FCSTD DOCUMENT  (FreeCAD 1.0R39109 (Git))
Label: TriggerPlateAssembly
License: All rights reserved
LicenseURL: http://en.wikipedia.org/wiki/All_rights_reserved
objects: App::Link×11, App::Part×1
EXTERNAL_REF file=../../ReferenceParts/KW-12.FCStd obj=Part
EXTERNAL_REF file=../../ReferenceParts/M3.FCStd obj=Part
EXTERNAL_REF file=../../ReferenceParts/M2.FCStd obj=Part
EXTERNAL_REF file=TriggerPlate.stl.FCStd obj=Part001
EXTERNAL_REF file=TriggerAssembly.FCStd obj=Assembly
EXTERNAL_REF file=LoadingLeverAssembly.FCStd obj=Part

FEATURE [App::Link] Link008  label="KW-12-25mm - Loading"
  LinkPlacement = pos=(48,-22,0) rot=(0,0,1;0.349066rad)
  LinkedObject = -> <external ../../ReferenceParts/KW-12.FCStd>#Part
  Placement = pos=(48,-22,0) rot=(0,0,1;0.349066rad)
FEATURE [App::Link] Link009  label="KW-12-25mm - Trigger"
  LinkPlacement = pos=(14,-11,2e-16) rot=(0,0,1;2.87979rad)
  LinkedObject = -> <external ../../ReferenceParts/KW-12.FCStd>#Part
  Placement = pos=(14,-11,2e-16) rot=(0,0,1;2.87979rad)
FEATURE [App::Link] Link  label="M3x10"
  LinkPlacement = pos=(30,-36,3.2) rot=(0,0,1;3.14159rad)
  LinkedObject = -> <external ../../ReferenceParts/M3.FCStd>#Part
  Placement = pos=(30,-36,3.2) rot=(0,0,1;3.14159rad)
FEATURE [App::Link] Link010  label="M3x011"
  LinkPlacement = pos=(35,-6,3.2) rot=(0,0,1;3.14177rad)
  LinkedObject = -> <external ../../ReferenceParts/M3.FCStd>#Part
  Placement = pos=(35,-6,3.2) rot=(0,0,1;3.14177rad)
FEATURE [App::Link] Link016  label="M2x10"
  LinkPlacement = pos=(8.66128,-12.5718,3.25) rot=(0,0,-1;0.261799rad)
  LinkedObject = -> <external ../../ReferenceParts/M2.FCStd>#Part
  Placement = pos=(8.66128,-12.5718,3.25) rot=(0,0,-1;0.261799rad)
FEATURE [App::Link] TriggerPlate_stl  label="TriggerPlate.stl001"
  LinkedObject = -> <external TriggerPlate.stl.FCStd>#Part001
FEATURE [App::Link] Link017  label="TriggerAssembly"
  LinkPlacement = pos=(30,-36,0.2) rot=(0,0,1;0rad)
  LinkedObject = -> <external TriggerAssembly.FCStd>#Assembly
  Placement = pos=(30,-36,0.2) rot=(0,0,1;0rad)
FEATURE [App::Link] M2x10  label="M2x011"
  LinkPlacement = pos=(17.8376,-15.0306,3.25) rot=(0,0,1;2.87979rad)
  LinkedObject = -> <external ../../ReferenceParts/M2.FCStd>#Part
  Placement = pos=(17.8376,-15.0306,3.25) rot=(0,0,1;2.87979rad)
FEATURE [App::Link] M2x011  label="M2x012"
  LinkPlacement = pos=(42.5446,-20.8995,3.25) rot=(0,0,1;0.349066rad)
  LinkedObject = -> <external ../../ReferenceParts/M2.FCStd>#Part
  Placement = pos=(42.5446,-20.8995,3.25) rot=(0,0,1;0.349066rad)
FEATURE [App::Link] M2x012  label="M2x013"
  LinkPlacement = pos=(51.4717,-17.6503,3.25) rot=(0,0,1;3.49066rad)
  LinkedObject = -> <external ../../ReferenceParts/M2.FCStd>#Part
  Placement = pos=(51.4717,-17.6503,3.25) rot=(0,0,1;3.49066rad)
FEATURE [App::Link] Link018  label="LoadingLeverAssembly"
  LinkPlacement = pos=(35,-6,0) rot=(0,0,1;0rad)
  LinkedObject = -> <external LoadingLeverAssembly.FCStd>#Part
  Placement = pos=(35,-6,0) rot=(0,0,1;0rad)
FEATURE [App::Part] Part  label="TriggerPlateAssembly"
  Group = -> [Link,Link009,Link016,Link010,Link008,TriggerPlate_stl,Link017,M2x10,M2x011,M2x012,Link018]
  Origin = -> Origin

RESOLVED EXTERNAL PARTS (link-assembly join: the EXTERNAL_REF files above that resolve inside this repo's crawl, each included once):
---- part ../../ReferenceParts/KW-12.FCStd = doc fcstd_e4d357ee2f76 ----
FCSTD DOCUMENT  (FreeCAD 1.0R39109 (Git))
Label: KW-12
License: All rights reserved
LicenseURL: http://en.wikipedia.org/wiki/All_rights_reserved
objects: Sketcher::SketchObject×6, PartDesign::Body×6, PartDesign::Pad×5, PartDesign::Mirrored×2, PartDesign::FeatureBase×2, PartDesign::Pocket×1, App::Part×1
note: 44 computed .brp shape members not serialized (recipe doc carries the construction recipe); baked Part::Feature solids carry a one-line shape summary decoded from their .brp

FEATURE [Sketcher::SketchObject] Sketch
  ArcFitTolerance = 1e-06
  AttachmentSupport = -> [XY_Plane]
  FullyConstrained = true
  MakeInternals = false
  MapMode = 5
  sketch-geometry (16):
    g0: LineSegment StartX=10 StartY=0.4 StartZ=0 EndX=10 EndY=10.4 EndZ=0
    g1: LineSegment StartX=-10 StartY=10 StartZ=0 EndX=-10 EndY=0.4 EndZ=0
    g2: LineSegment StartX=10 StartY=10.4 StartZ=0 EndX=-1.2008e-12 EndY=10.4 EndZ=0
    g3: LineSegment StartX=-1.2011e-12 StartY=10.4 StartZ=0 EndX=-1.2011e-12 EndY=10 EndZ=0
    g4: LineSegment StartX=-1.2011e-12 StartY=10 StartZ=0 EndX=-10 EndY=10 EndZ=0
    g5: LineSegment StartX=-10 StartY=0.4 StartZ=0 EndX=-6.75 EndY=0.4 EndZ=0
    g6: LineSegment StartX=-6.75 StartY=0.4 StartZ=0 EndX=-6.75 EndY=1.2024e-12 EndZ=0
    g7: LineSegment StartX=-6.75 StartY=1.2024e-12 StartZ=0 EndX=-2.75 EndY=1.2024e-12 EndZ=0
    g8: LineSegment StartX=-2.75 StartY=1.2024e-12 StartZ=0 EndX=-2.75 EndY=0.4 EndZ=0
    g9: LineSegment StartX=-2.75 StartY=0.4 StartZ=0 EndX=2.75 EndY=0.4 EndZ=0
    g10: LineSegment StartX=2.75 StartY=0.4 StartZ=0 EndX=2.75 EndY=-1.2024e-12 EndZ=0
    g11: LineSegment StartX=2.75 StartY=-1.2024e-12 StartZ=0 EndX=6.75 EndY=-1.2024e-12 EndZ=0
    g12: LineSegment StartX=6.75 StartY=-1.2024e-12 StartZ=0 EndX=6.75 EndY=0.4 EndZ=0
    g13: LineSegment StartX=6.75 StartY=0.4 StartZ=0 EndX=10 EndY=0.4 EndZ=0
    g14: GeomPoint X=-4.75 Y=1.2024e-12 Z=0
    g15: GeomPoint X=-4.75 Y=2.9 Z=0
  constraints (44):
    c: Vertical(g0)
    c: Vertical(g1)
    c: Coincident(g2,g0)
    c: Horizontal(g2)
    c: Coincident(g3,g2)
    c: Vertical(g3)
    c: Coincident(g4,g1)
    c: Horizontal(g4)
    c: Coincident(g3,g4)
    c: DistanceX(g2,g2) = 10
    c: Coincident(g5,g1)
    c: Coincident(g5,g6)
    c: Coincident(g6,g7)
    c: Horizontal(g7)
    c: Coincident(g7,g8)
    c: Vertical(g8)
    c: Coincident(g8,g9)
    c: Coincident(g9,g10)
    c: Vertical(g10)
    c: Coincident(g10,g11)
    c: Horizontal(g11)
    c: Coincident(g11,g12)
    c: Vertical(g12)
    c: Coincident(g12,g13)
    c: Coincident(g13,g0)
    c: Horizontal(g13)
    c: Equal(g11,g7)
    c: Vertical(g6)
    c: DistanceX(g7,g7) = 4
    c: Equal(g10,g8)
    c: Horizontal(g5)
    c: DistanceY(g1,g1) = 9.6
    c: Horizontal(g9)
    c: Horizontal(g9,g12)
    c: Horizontal(g5,g8)
    c: DistanceX(g1,g0) = 20
    c: Equal(g5,g13)
    c: Symmetric(g7,g10,g-1)
    c: Symmetric(g7,g6,g14)
    c: DistanceX(g14,g-1) = 4.75
    c: DistanceY(g-1,g0) = 10.4
    c: DistanceY(g-1,g15) = 2.9
    c: DistanceX(g15,g-1) = 4.75
    c: DistanceY(g5,g15) = 2.5
FEATURE [PartDesign::Pad] Pad
  Direction = (0,0,1)
  Length = 6.3
  Length2 = 10
  Midplane = true
  Profile = -> Sketch
  ReferenceAxis = -> Sketch [N_Axis]
  Refine = true
  Suppressed = false
  Type = 0
FEATURE [Sketcher::SketchObject] Sketch001
  ArcFitTolerance = 1e-06
  AttachmentSupport = -> [XY_Plane]
  FullyConstrained = true
  MakeInternals = false
  MapMode = 5
  sketch-geometry (4):
    g0: LineSegment StartX=-2.5 StartY=2.9 StartZ=0 EndX=-2.5 EndY=0.5 EndZ=0
    g1: LineSegment StartX=-2.5 StartY=0.5 StartZ=0 EndX=-7 EndY=0.5 EndZ=0
    g2: LineSegment StartX=-7 StartY=0.5 StartZ=0 EndX=-7 EndY=2.9 EndZ=0
    g3: ArcOfCircle CenterX=-4.75 CenterY=2.9 CenterZ=0 NormalX=0 NormalY=0 NormalZ=1 AngleXU=0 Radius=2.25 StartAngle=8.70301e-11 EndAngle=3.14159
  constraints (12):
    c: Coincident(g0,g1)
    c: Horizontal(g1)
    c: Coincident(g1,g2)
    c: Vertical(g2)
    c: Tangent(g2,g3) = 1.5708
    c: Coincident(g3,g0)
    c: Vertical(g0)
    c: Horizontal(g0,g2)
    c: Radius(g3) = 2.25
    c: DistanceX(g3,g-1) = 4.75
    c: DistanceY(g-1,g0) = 0.5
    c: DistanceY(g-1,g2) = 2.9
FEATURE [PartDesign::Pad] Pad001
  BaseFeature = -> Pad
  Direction = (0,0,1)
  Length = 6.5
  Length2 = 10
  Midplane = true
  Profile = -> Sketch001
  ReferenceAxis = -> Sketch001 [N_Axis]
  Refine = true
  Suppressed = false
  Type = 0
FEATURE [PartDesign::Mirrored] Mirrored
  BaseFeature = -> Pad001
  MirrorPlane = -> Sketch001 [V_Axis]
  Originals = -> [Pad001]
  Refine = true
  Suppressed = false
  TransformMode = 0
FEATURE [Sketcher::SketchObject] Sketch002
  ArcFitTolerance = 1e-06
  AttachmentSupport = -> [XY_Plane]
  FullyConstrained = true
  MakeInternals = false
  MapMode = 5
  sketch-geometry (1):
    g0: Circle CenterX=-4.75 CenterY=2.9 CenterZ=0 NormalX=0 NormalY=0 NormalZ=1 AngleXU=0 Radius=1.3
  constraints (3):
    c: DistanceY(g-1,g0) = 2.9
    c: DistanceX(g0,g-1) = 4.75
    c: Diameter(g0) = 2.6
FEATURE [PartDesign::Pocket] Pocket
  BaseFeature = -> Mirrored
  Direction = (0,0,-1)
  Length = 5
  Length2 = 5
  Midplane = true
  Profile = -> Sketch002
  ReferenceAxis = -> Sketch002 [N_Axis]
  Refine = true
  Suppressed = false
  Type = 1
FEATURE [Sketcher::SketchObject] Sketch003
  ArcFitTolerance = 1e-06
  AttachmentSupport = -> [XY_Plane001]
  FullyConstrained = true
  MakeInternals = false
  MapMode = 5
  sketch-geometry (5):
    g0: LineSegment StartX=2 StartY=11 StartZ=0 EndX=2 EndY=9 EndZ=0
    g1: LineSegment StartX=2 StartY=9 StartZ=0 EndX=4 EndY=9 EndZ=0
    g2: LineSegment StartX=4 StartY=9 StartZ=0 EndX=4 EndY=11 EndZ=0
    g3: ArcOfCircle CenterX=3 CenterY=11 CenterZ=0 NormalX=0 NormalY=0 NormalZ=1 AngleXU=0 Radius=1 StartAngle=-3.8529e-12 EndAngle=3.14159
    g4: GeomPoint X=3 Y=12 Z=0
  constraints (13):
    c: Vertical(g0)
    c: Coincident(g0,g1)
    c: Horizontal(g1)
    c: Coincident(g1,g2)
    c: Vertical(g2)
    c: Tangent(g2,g3) = -1.5708
    c: DistanceX(g-1,g1) = 4
    c: DistanceX(g1,g1) = 2
    c: DistanceY(g0,g0) = 2
    c: Tangent(g3,g0) = -1.5708
    c: PointOnObject(g4,g3)
    c: Vertical(g4,g3)
    c: DistanceY(g-1,g4) = 12
FEATURE [PartDesign::Pad] Pad002
  Direction = (0,0,1)
  Length = 4
  Length2 = 10
  Midplane = true
  Profile = -> Sketch003
  ReferenceAxis = -> Sketch003 [N_Axis]
  Refine = true
  Suppressed = false
  Type = 0
FEATURE [PartDesign::Body] Body001  label="Toggle"
  AllowCompound = false
  Group = -> [Sketch003,Pad002]
  Origin = -> Origin001
  Tip = -> Pad002
FEATURE [Sketcher::SketchObject] Sketch004
  ArcFitTolerance = 1e-06
  AttachmentSupport = -> [XY_Plane003]
  FullyConstrained = true
  MakeInternals = false
  MapMode = 5
  sketch-geometry (15):
    g0: LineSegment StartX=-8.2 StartY=-4 StartZ=0 EndX=-7.7 EndY=-4 EndZ=0
    g1: LineSegment StartX=-7.7 StartY=-4 StartZ=0 EndX=-7.7 EndY=1 EndZ=0
    g2: LineSegment StartX=-8.2 StartY=1.5 StartZ=0 EndX=-8.2 EndY=-4 EndZ=0
    g3: LineSegment StartX=-1 StartY=-4 StartZ=0 EndX=-0.5 EndY=-4 EndZ=0
    g4: LineSegment StartX=-0.5 StartY=-4 StartZ=0 EndX=-0.5 EndY=1 EndZ=0
    g5: LineSegment StartX=-1 StartY=1 StartZ=0 EndX=-1 EndY=-4 EndZ=0
    g6: LineSegment StartX=7.7 StartY=-4 StartZ=0 EndX=8.2 EndY=-4 EndZ=0
    g7: LineSegment StartX=8.2 StartY=-4 StartZ=0 EndX=8.2 EndY=1.5 EndZ=0
    g8: LineSegment StartX=7.7 StartY=1 StartZ=0 EndX=7.7 EndY=-4 EndZ=0
    g9: GeomPoint X=-7.95 Y=-4 Z=0
    g10: GeomPoint X=-0.75 Y=-4 Z=0
    g11: GeomPoint X=7.95 Y=-4 Z=0
    g12: LineSegment StartX=-0.5 StartY=1 StartZ=0 EndX=7.7 EndY=1 EndZ=0
    g13: LineSegment StartX=-7.7 StartY=1 StartZ=0 EndX=-1 EndY=1 EndZ=0
    g14: LineSegment StartX=-8.2 StartY=1.5 StartZ=0 EndX=8.2 EndY=1.5 EndZ=0
  constraints (38):
    c: Coincident(g0,g1)
    c: Coincident(g2,g0)
    c: Horizontal(g0)
    c: Vertical(g1)
    c: Vertical(g2)
    c: Coincident(g3,g4)
    c: Coincident(g5,g3)
    c: Horizontal(g3)
    c: Vertical(g4)
    c: Vertical(g5)
    c: Coincident(g6,g7)
    c: Coincident(g8,g6)
    c: Horizontal(g6)
    c: Vertical(g7)
    c: Vertical(g8)
    c: Horizontal(g6,g3)
    c: Equal(g0,g3)
    c: Equal(g3,g6)
    c: DistanceX(g6,g6) = 0.5
    c: Symmetric(g0,g0,g9)
    c: Symmetric(g3,g3,g10)
    c: Symmetric(g6,g6,g11)
    c: DistanceX(g10,g11) = 8.7
    c: DistanceX(g9,g10) = 7.2
    c: Symmetric(g9,g11,g-2)
    c: Coincident(g12,g4)
    c: Coincident(g12,g8)
    c: Horizontal(g12)
    c: Coincident(g13,g1)
    c: Coincident(g13,g5)
    c: Horizontal(g13)
    c: Coincident(g14,g2)
    c: Coincident(g14,g7)
    c: Horizontal(g14)
    c: Horizontal(g5,g4)
    c: DistanceY(g-1,g8) = 1
    c: DistanceY(g8,g7) = 0.5
    c: DistanceY(g0,g-1) = 4
FEATURE [PartDesign::Pad] Pad003
  Direction = (0,0,1)
  Length = 3.5
  Length2 = 10
  Midplane = true
  Profile = -> Sketch004
  ReferenceAxis = -> Sketch004 [N_Axis]
  Refine = true
  Suppressed = false
  Type = 0
FEATURE [PartDesign::Body] Body002  label="Legs"
  AllowCompound = false
  Group = -> [Sketch004,Pad003]
  Origin = -> Origin003
  Tip = -> Pad003
FEATURE [Sketcher::SketchObject] Sketch005
  ArcFitTolerance = 1e-06
  AttachmentSupport = -> [XY_Plane004]
  FullyConstrained = true
  MakeInternals = false
  MapMode = 5
  sketch-geometry (6):
    g0: LineSegment StartX=0 StartY=0 StartZ=0 EndX=0 EndY=1.5 EndZ=0
    g1: LineSegment StartX=0 StartY=1.5 StartZ=0 EndX=-24.5 EndY=1.5 EndZ=0
    g2: LineSegment StartX=-24.5 StartY=1.5 StartZ=0 EndX=-24.5 EndY=2 EndZ=0
    g3: LineSegment StartX=-24.5 StartY=2 StartZ=0 EndX=0.5 EndY=2 EndZ=0
    g4: LineSegment StartX=0.5 StartY=2 StartZ=0 EndX=0.5 EndY=0 EndZ=0
    g5: LineSegment StartX=0.5 StartY=0 StartZ=0 EndX=0 EndY=0 EndZ=0
  constraints (17):
    c: Coincident(g-1,g0)
    c: PointOnObject(g0,g-2)
    c: Coincident(g0,g1)
    c: Horizontal(g1)
    c: Coincident(g1,g2)
    c: Coincident(g2,g3)
    c: Horizontal(g3)
    c: Coincident(g3,g4)
    c: PointOnObject(g4,g-1)
    c: Vertical(g4)
    c: Coincident(g4,g5)
    c: Coincident(g5,g0)
    c: Vertical(g2)
    c: DistanceY(g2,g2) = 0.5
    c: DistanceX(g3,g3) = 25
    c: DistanceX(g0,g3) = 0.5
    c: DistanceY(g4,g4) = 2
FEATURE [PartDesign::Pad] Pad004
  Direction = (0,0,1)
  Length = 4.2
  Length2 = 10
  Midplane = true
  Profile = -> Sketch005
  ReferenceAxis = -> Sketch005 [N_Axis]
  Refine = true
  Suppressed = false
  Type = 0
FEATURE [PartDesign::Body] Body003  label="SwitchLever25mm-Trigger"
  AllowCompound = false
  Group = -> [Sketch005,Pad004]
  Origin = -> Origin004
  Placement = pos=(6.5,9.5,0) rot=(0,0,1;0rad)
  Tip = -> Pad004
FEATURE [PartDesign::FeatureBase] Clone
  BaseFeature = -> Body003
  Suppressed = false
FEATURE [PartDesign::Body] Body004  label="SwitchLever25mm-Neutral"
  AllowCompound = false
  Group = -> [Clone]
  Origin = -> Origin005
  Placement = pos=(6.5,9.5,0) rot=(0,0,1;6.02139rad)
  Tip = -> Clone
FEATURE [PartDesign::FeatureBase] Clone001
  BaseFeature = -> Body003
  Suppressed = false
FEATURE [PartDesign::Body] Body005  label="SwitchLever25mm-Depressed"
  AllowCompound = false
  Group = -> [Clone001]
  Origin = -> Origin006
  Placement = pos=(6.5,9.5,0) rot=(0,0,-1;6.2221rad)
  Tip = -> Clone001
FEATURE [PartDesign::Mirrored] Mirrored001
  BaseFeature = -> Pocket
  MirrorPlane = -> Sketch002 [V_Axis]
  Originals = -> [Pocket]
  Refine = true
  Suppressed = false
  TransformMode = 0
FEATURE [PartDesign::Body] Body  label="Housing"
  AllowCompound = false
  Group = -> [Sketch,Pad,Sketch001,Pad001,Mirrored,Sketch002,Pocket,Mirrored001]
  Origin = -> Origin
  Tip = -> Mirrored001
FEATURE [App::Part] Part  label="KW-12-25mm"
  Group = -> [Body,Body001,Body002,Body003,Body004,Body005]
  Origin = -> Origin002
---- part LoadingLeverAssembly.FCStd = doc fcstd_2eb7aa16ae78 ----
FCSTD DOCUMENT  (FreeCAD 1.0R39109 (Git))
Label: LoadingLeverAssembly
License: All rights reserved
LicenseURL: http://en.wikipedia.org/wiki/All_rights_reserved
objects: App::Link×5, App::Part×1
EXTERNAL_REF file=TriggerPivotBusing.stl.FCStd obj=Part
EXTERNAL_REF file=LoadingLever.stl.FCStd obj=Part
EXTERNAL_REF file=../LoadingLeverGrip.stl.FCStd obj=Part
EXTERNAL_REF file=../../ReferenceParts/M3.FCStd obj=Part

FEATURE [App::Link] Link015  label="LoadingPivotBushing"
  LinkPlacement = pos=(0,7e-16,3) rot=(1,0,0;3.14159rad)
  LinkedObject = -> <external TriggerPivotBusing.stl.FCStd>#Part
  Placement = pos=(0,7e-16,3) rot=(1,0,0;3.14159rad)
FEATURE [App::Link] Link012  label="LoadingLever.stl"
  LinkedObject = -> <external LoadingLever.stl.FCStd>#Part
FEATURE [App::Link] Link  label="LoadingLeverGrip.stl"
  LinkPlacement = pos=(8.25,6,-1.69873e-06) rot=(-0.57735,-0.57735,0.57735;4.18879rad)
  LinkedObject = -> <external ../LoadingLeverGrip.stl.FCStd>#Part
  Placement = pos=(8.25,6,-1.69873e-06) rot=(-0.57735,-0.57735,0.57735;4.18879rad)
FEATURE [App::Link] Link016  label="M3x10"
  LinkPlacement = pos=(12,2,8) rot=(0,0,1;0rad)
  LinkedObject = -> <external ../../ReferenceParts/M3.FCStd>#Part
  Placement = pos=(12,2,8) rot=(0,0,1;0rad)
FEATURE [App::Link] Link017  label="M3x011"
  LinkPlacement = pos=(30,2,-8) rot=(0,1,0;3.14159rad)
  LinkedObject = -> Link016
  Placement = pos=(30,2,-8) rot=(0,1,0;3.14159rad)
FEATURE [App::Part] Part  label="LoadingLeverAssembly"
  Group = -> [Link012,Link015,Link,Link016,Link017]
  Origin = -> Origin
---- part TriggerAssembly.FCStd = doc fcstd_4eb5c5076385 ----
FCSTD DOCUMENT  (FreeCAD 1.0R39109 (Git))
Label: TriggerAssembly
License: All rights reserved
LicenseURL: http://en.wikipedia.org/wiki/All_rights_reserved
objects: App::Link×5, App::FeaturePython×5, Assembly::JointGroup×1, Assembly::AssemblyObject×1
EXTERNAL_REF file=TriggerPivotBusing.stl.FCStd obj=Part
EXTERNAL_REF file=Trigger.stl.FCStd obj=Part001
EXTERNAL_REF file=../../ReferenceParts/M3.FCStd obj=Part

FEATURE [App::Link] Link014  label="TriggerPivotBushing"
  LinkPlacement = pos=(0,7e-16,3) rot=(-1,0,0;3.14159rad)
  LinkedObject = -> <external TriggerPivotBusing.stl.FCStd>#Part
  Placement = pos=(0,7e-16,3) rot=(-1,0,0;3.14159rad)
FEATURE [App::Link] Trigger_stl  label="Trigger.stl"
  LinkedObject = -> <external Trigger.stl.FCStd>#Part001
FEATURE [App::FeaturePython] GroundedJoint  # Assembly grounded joint (typed FeaturePython)
  ObjectToGround = -> Trigger_stl
FEATURE [App::FeaturePython] Joint  label="Fixed"  # Assembly joint (typed FeaturePython)
  Activated = true
  AngleMax = 0
  AngleMin = 0
  Detach1 = false
  Detach2 = false
  Distance = 0
  Distance2 = 0
  EnableAngleMax = false
  EnableAngleMin = false
  EnableLengthMax = false
  EnableLengthMin = false
  JointType = 0 (Fixed)
  LengthMax = 0
  LengthMin = 0
  Placement1 = pos=(0,3e-16,1.5) rot=(0,0,1;3.14159rad)
  Placement2 = pos=(0,3e-16,1.5) rot=(0,1,0;3.14159rad)
  Reference1 = -> Assembly [Link014.Body.Edge3,Link014.Body.Edge3]
  Reference2 = -> Assembly [Trigger_stl.Body.Edge63,Trigger_stl.Body.Edge63]
FEATURE [App::Link] M3x10  label="M3x011"
  LinkPlacement = pos=(-10.3581,0.779318,2.07e-14) rot=(0.970288,-0.171088,-0.171088;1.60095rad)
  LinkedObject = -> <external ../../ReferenceParts/M3.FCStd>#Part
  Placement = pos=(-10.3581,0.779318,2.07e-14) rot=(0.970288,-0.171088,-0.171088;1.60095rad)
FEATURE [App::Link] M3x011  label="M3x012"
  LinkPlacement = pos=(-18,2.55146,-6e-16) rot=(1,0,0;1.5708rad)
  LinkedObject = -> <external ../../ReferenceParts/M3.FCStd>#Part
  Placement = pos=(-18,2.55146,-6e-16) rot=(1,0,0;1.5708rad)
FEATURE [App::Link] M3x012  label="M3x013"
  LinkPlacement = pos=(25,-4,9e-16) rot=(1,0,0;1.5708rad)
  LinkedObject = -> <external ../../ReferenceParts/M3.FCStd>#Part
  Placement = pos=(25,-4,9e-16) rot=(1,0,0;1.5708rad)
FEATURE [App::FeaturePython] Joint002  label="Fixed002"  # Assembly joint (typed FeaturePython)
  Activated = true
  AngleMax = 0
  AngleMin = 0
  Detach1 = false
  Detach2 = false
  Distance = 0
  Distance2 = 0
  EnableAngleMax = false
  EnableAngleMin = false
  EnableLengthMax = false
  EnableLengthMin = false
  JointType = 0 (Fixed)
  LengthMax = 0
  LengthMin = 0
  Offset2 = pos=(0,0,6) rot=(0,0,1;0rad)
  Placement2 = pos=(-10.3581,0.779318,2.07e-14) rot=(0.970288,-0.171088,-0.171088;1.60095rad)
  Reference1 = -> Assembly [M3x10.Screw.Edge30,M3x10.Screw.Edge30]
  Reference2 = -> Assembly [Trigger_stl.Body.Edge30,Trigger_stl.Body.Edge30]
FEATURE [App::FeaturePython] Joint003  label="Fixed003"  # Assembly joint (typed FeaturePython)
  Activated = true
  AngleMax = 0
  AngleMin = 0
  Detach1 = false
  Detach2 = false
  Distance = 0
  Distance2 = 0
  EnableAngleMax = false
  EnableAngleMin = false
  EnableLengthMax = false
  EnableLengthMin = false
  JointType = 0 (Fixed)
  LengthMax = 0
  LengthMin = 0
  Offset2 = pos=(0,0,6) rot=(0,0,1;0rad)
  Placement2 = pos=(-18,2.55146,-6e-16) rot=(1,0,0;1.5708rad)
  Reference1 = -> Assembly [M3x011.Screw.Edge30,M3x011.Screw.Edge30]
  Reference2 = -> Assembly [Trigger_stl.Body.Edge5,Trigger_stl.Body.Edge5]
FEATURE [App::FeaturePython] Joint004  label="Fixed004"  # Assembly joint (typed FeaturePython)
  Activated = true
  AngleMax = 0
  AngleMin = 0
  Detach1 = false
  Detach2 = false
  Distance = 0
  Distance2 = 0
  EnableAngleMax = false
  EnableAngleMin = false
  EnableLengthMax = false
  EnableLengthMin = false
  JointType = 0 (Fixed)
  LengthMax = 0
  LengthMin = 0
  Offset2 = pos=(0,0,6) rot=(0,0,1;0rad)
  Placement2 = pos=(25,-4,9e-16) rot=(1,0,0;1.5708rad)
  Reference1 = -> Assembly [M3x012.Screw.Edge30,M3x012.Screw.Edge30]
  Reference2 = -> Assembly [Trigger_stl.Body.Edge40,Trigger_stl.Body.Edge40]
FEATURE [Assembly::JointGroup] Joints
  Group = -> [GroundedJoint,Joint,Joint002,Joint003,Joint004]
FEATURE [Assembly::AssemblyObject] Assembly  label="TriggerAssembly"
  Group = -> [Joints,Link014,Trigger_stl,GroundedJoint,Joint,M3x10,M3x011,M3x012,Joint002,Joint003,Joint004]
  Origin = -> Origin007
  Type = Assembly
---- part TriggerPlate.stl.FCStd = doc fcstd_9ce144a7f0ca ----
FCSTD DOCUMENT  (FreeCAD 1.0R39109 (Git))
Label: TriggerPlate.stl
License: All rights reserved
LicenseURL: http://en.wikipedia.org/wiki/All_rights_reserved
objects: Sketcher::SketchObject×11, PartDesign::Pocket×10, PartDesign::SubShapeBinder×4, PartDesign::Pad×3, PartDesign::Body×1, App::Part×1
note: 66 computed .brp shape members not serialized (recipe doc carries the construction recipe); baked Part::Feature solids carry a one-line shape summary decoded from their .brp

FEATURE [Sketcher::SketchObject] Sketch
  ArcFitTolerance = 1e-06
  AttachmentOffset = pos=(0,0,-6.75) rot=(0,0,1;0rad)
  AttachmentSupport = -> [XY_Plane003]
  FullyConstrained = true
  MakeInternals = false
  MapMode = 5
  Placement = pos=(0,0,-6.75) rot=(0,0,1;0rad)
  sketch-geometry (7):
    g0: LineSegment StartX=0.25 StartY=-35 StartZ=0 EndX=26.3744 EndY=-42 EndZ=0
    g1: Circle CenterX=5 CenterY=-25 CenterZ=0 NormalX=0 NormalY=0 NormalZ=1 AngleXU=0 Radius=1.25
    g2: Circle CenterX=65 CenterY=-25 CenterZ=0 NormalX=0 NormalY=0 NormalZ=1 AngleXU=0 Radius=1.25
    g3: LineSegment StartX=26.3744 StartY=-42 StartZ=0 EndX=69.75 EndY=-42 EndZ=0
    g4: LineSegment StartX=69.75 StartY=0 StartZ=0 EndX=69.75 EndY=-42 EndZ=0
    g5: LineSegment StartX=0.25 StartY=-35 StartZ=0 EndX=0.25 EndY=0 EndZ=0
    g6: LineSegment StartX=69.75 StartY=0 StartZ=0 EndX=0.25 EndY=0 EndZ=0
  constraints (21):
    c: DistanceY(g0,g-1) = 35
    c: Diameter(g1) = 2.5
    c: DistanceX(g-1,g1) = 5
    c: DistanceY(g1,g-1) = 25
    c: Equal(g2,g1)
    c: DistanceX(g1,g2) = 60
    c: Horizontal(g1,g2)
    c: Coincident(g3,g0)
    c: Horizontal(g3)
    c: Coincident(g4,g3)
    c: Vertical(g4)
    c: Distance(g0,g-2) = 0.25
    c: Coincident(g5,g0)
    c: Coincident(g6,g4)
    c: Coincident(g6,g5)
    c: Vertical(g5)
    c: Angle(g0,g5) = 1.8326
    c: DistanceX(g6,g6) = 69.5
    c: Horizontal(g6)
    c: DistanceY(g3,g-1) = 42
    c: PointOnObject(g4,g-1)
FEATURE [PartDesign::Pad] Pad
  Direction = (0,0,1)
  Length = 13
  Length2 = 10
  Profile = -> Sketch
  ReferenceAxis = -> Sketch [N_Axis]
  Refine = true
  Suppressed = false
  Type = 0
FEATURE [Sketcher::SketchObject] Sketch001
  ArcFitTolerance = 1e-06
  AttachmentOffset = pos=(0,0,-4.5) rot=(0,0,1;0rad)
  AttachmentSupport = -> [XY_Plane003]
  FullyConstrained = true
  MakeInternals = false
  MapMode = 5
  Placement = pos=(0,0,-4.5) rot=(0,0,1;0rad)
  sketch-geometry (6):
    g0: ArcOfCircle CenterX=30 CenterY=-36 CenterZ=0 NormalX=0 NormalY=0 NormalZ=1 AngleXU=0 Radius=24 StartAngle=2.56917 EndAngle=4.71239
    g1: ArcOfCircle CenterX=30 CenterY=-36 CenterZ=0 NormalX=0 NormalY=0 NormalZ=1 AngleXU=0 Radius=30 StartAngle=4.71239 EndAngle=6.48454
    g2: LineSegment StartX=30 StartY=-60 StartZ=0 EndX=30 EndY=-66 EndZ=0
    g3: LineSegment StartX=35.6077 StartY=-30 StartZ=0 EndX=59.3939 EndY=-30 EndZ=0
    g4: LineSegment StartX=35.6077 StartY=-30 StartZ=0 EndX=23.4833 EndY=-23 EndZ=0
    g5: LineSegment StartX=23.4833 StartY=-23 StartZ=0 EndX=9.82576 EndY=-23 EndZ=0
  constraints (19):
    c: Coincident(g1,g0)
    c: Coincident(g2,g0)
    c: Coincident(g2,g1)
    c: Coincident(g3,g1)
    c: Horizontal(g3)
    c: Radius(g1) = 30
    c: Radius(g0) = 24
    c: DistanceX(g-1,g0) = 30
    c: DistanceY(g0,g-1) = 36
    c: DistanceY(g0,g1) = 6
    c: Vertical(g2)
    c: Vertical(g0,g0)
    c: Coincident(g4,g3)
    c: Coincident(g5,g4)
    c: Coincident(g5,g0)
    c: Horizontal(g5)
    c: Distance(g0,g4) = 8
    c: Angle(g4,g3) = 0.523599
    c: DistanceY(g0,g0) = 13
FEATURE [PartDesign::Pocket] Pocket  label="TriggerCutout"
  BaseFeature = -> Pad
  Direction = (0,0,-1)
  Length = 5
  Length2 = 5
  Profile = -> Sketch001
  ReferenceAxis = -> Sketch001 [N_Axis]
  Refine = true
  Reversed = true
  Suppressed = false
  Type = 1
FEATURE [Sketcher::SketchObject] Sketch002
  ArcFitTolerance = 1e-06
  AttachmentOffset = pos=(0,0,-4) rot=(0,0,1;0rad)
  AttachmentSupport = -> [XY_Plane003]
  FullyConstrained = true
  MakeInternals = false
  MapMode = 5
  Placement = pos=(0,0,-4) rot=(0,0,1;0rad)
  sketch-geometry (1):
    g0: Circle CenterX=30 CenterY=-36 CenterZ=0 NormalX=0 NormalY=0 NormalZ=1 AngleXU=0 Radius=5
  constraints (3):
    c: DistanceX(g-1,g0) = 30
    c: DistanceY(g0,g-1) = 36
    c: Diameter(g0) = 10
FEATURE [PartDesign::Pad] Pad001  label="TriggerBush"
  BaseFeature = -> Pocket
  Direction = (0,0,1)
  Length = 10
  Length2 = 10
  Profile = -> Sketch002
  ReferenceAxis = -> Sketch002 [N_Axis]
  Refine = true
  Reversed = true
  Suppressed = false
  Type = 2
FEATURE [Sketcher::SketchObject] Sketch003
  ArcFitTolerance = 1e-06
  AttachmentSupport = -> [XY_Plane003]
  FullyConstrained = true
  MakeInternals = false
  MapMode = 5
  sketch-geometry (1):
    g0: Circle CenterX=30 CenterY=-36 CenterZ=0 NormalX=0 NormalY=0 NormalZ=1 AngleXU=0 Radius=1.25
  constraints (3):
    c: DistanceX(g-1,g0) = 30
    c: DistanceY(g0,g-1) = 36
    c: Diameter(g0) = 2.5
FEATURE [PartDesign::Pocket] Pocket001  label="TriggerBoltHole"
  BaseFeature = -> Pad001
  Direction = (0,0,-1)
  Length = 5
  Length2 = 5
  Midplane = true
  Profile = -> Sketch003
  ReferenceAxis = -> Sketch003 [N_Axis]
  Refine = true
  Suppressed = false
  Type = 1
FEATURE [Sketcher::SketchObject] Sketch004
  ArcFitTolerance = 1e-06
  AttachmentOffset = pos=(0,0,-4.5) rot=(0,0,1;0rad)
  AttachmentSupport = -> [XY_Plane003]
  FullyConstrained = true
  MakeInternals = false
  MapMode = 5
  Placement = pos=(0,0,-4.5) rot=(0,0,1;0rad)
  sketch-geometry (4):
    g0: ArcOfCircle CenterX=35 CenterY=-6 CenterZ=0 NormalX=0 NormalY=0 NormalZ=1 AngleXU=0 Radius=36 StartAngle=6.2276 EndAngle=7.20457
    g1: ArcOfCircle CenterX=35 CenterY=-6 CenterZ=0 NormalX=0 NormalY=0 NormalZ=1 AngleXU=0 Radius=11 StartAngle=2.18166 EndAngle=6.10035
    g2: LineSegment StartX=28.6907 StartY=3.01067 StartZ=0 EndX=56.7698 EndY=22.6719 EndZ=0
    g3: LineSegment StartX=45.8167 StartY=-8 StartZ=0 EndX=70.9444 EndY=-8 EndZ=0
  constraints (12):
    c: Coincident(g1,g0)
    c: Coincident(g2,g0)
    c: Coincident(g3,g1)
    c: Coincident(g3,g0)
    c: Horizontal(g3)
    c: DistanceY(g0,g-1) = 6
    c: DistanceX(g-1,g0) = 35
    c: DistanceY(g0,g0) = 2
    c: Radius(g1) = 11
    c: Tangent(g2,g1) = 1.5708
    c: Angle(g-1,g2) = 0.610865
    c: Radius(g0) = 36
FEATURE [PartDesign::Pocket] Pocket002  label="LoadingLeverCutout1"
  BaseFeature = -> Pocket001
  Direction = (0,0,-1)
  Length = 5
  Length2 = 5
  Profile = -> Sketch004
  ReferenceAxis = -> Sketch004 [N_Axis]
  Refine = true
  Reversed = true
  Suppressed = false
  Type = 1
FEATURE [Sketcher::SketchObject] Sketch005
  ArcFitTolerance = 1e-06
  AttachmentSupport = -> [XY_Plane003]
  FullyConstrained = true
  MakeInternals = false
  MapMode = 5
  sketch-geometry (5):
    g0: LineSegment StartX=75 StartY=-3.6e-15 StartZ=0 EndX=40.4584 EndY=-3.6e-15 EndZ=0
    g1: LineSegment StartX=46.9451 StartY=-8 StartZ=0 EndX=75 EndY=-8 EndZ=0
    g2: LineSegment StartX=75 StartY=-8 StartZ=0 EndX=75 EndY=-3.6e-15 EndZ=0
    g3: ArcOfCircle CenterX=46.9451 CenterY=-4 CenterZ=0 NormalX=0 NormalY=0 NormalZ=1 AngleXU=0 Radius=4 StartAngle=3.30749 EndAngle=4.71239
    g4: ArcOfCircle CenterX=35 CenterY=-6 CenterZ=0 NormalX=0 NormalY=0 NormalZ=1 AngleXU=0 Radius=8.11136 StartAngle=0.165894 EndAngle=0.832629
  constraints (15):
    c: Coincident(g1,g2)
    c: Coincident(g2,g0)
    c: Horizontal(g0)
    c: Horizontal(g1)
    c: Vertical(g2)
    c: PointOnObject(g0,g-1)
    c: Tangent(g1,g3) = -1.5708
    c: Radius(g3) = 4
    c: DistanceY(g1,g-1) = 8
    c: DistanceX(g-1,g0) = 75
    c: Coincident(g4,g0)
    c: DistanceX(g-1,g3) = 43
    c: DistanceY(g4,g-1) = 6
    c: DistanceX(g-1,g4) = 35
    c: Tangent(g4,g3) = 1.5708
FEATURE [PartDesign::Pocket] Pocket003  label="LoadingLeverCutout2"
  BaseFeature = -> Pocket002
  Direction = (0,0,-1)
  Length = 5
  Length2 = 5
  Midplane = true
  Profile = -> Sketch005
  ReferenceAxis = -> Sketch005 [N_Axis]
  Refine = true
  Suppressed = false
  Type = 1
FEATURE [Sketcher::SketchObject] Sketch006  label="KW-12CutoutBase"
  ArcFitTolerance = 1e-06
  AttachmentSupport = -> [XY_Plane004]
  FullyConstrained = true
  MakeInternals = false
  MapMode = 5
  sketch-geometry (7):
    g0: LineSegment StartX=-10.25 StartY=9.5 StartZ=0 EndX=-10.25 EndY=-6 EndZ=0
    g1: LineSegment StartX=-10.25 StartY=-6 StartZ=0 EndX=10.25 EndY=-6 EndZ=0
    g2: LineSegment StartX=10.25 StartY=-6 StartZ=0 EndX=10.25 EndY=11 EndZ=0
    g3: LineSegment StartX=10.25 StartY=11 StartZ=0 EndX=-18.4391 EndY=19.7712 EndZ=0
    g4: ArcOfCircle CenterX=10.25 CenterY=11 CenterZ=0 NormalX=0 NormalY=0 NormalZ=1 AngleXU=0 Radius=30 StartAngle=2.84489 EndAngle=3.20812
    g5: LineSegment StartX=-19.6836 StartY=9.0056 StartZ=0 EndX=-10.25 EndY=9.5 EndZ=0
    g6: GeomPoint [constr] X=10.25 Y=11 Z=0
  constraints (18):
    c: Coincident(g0,g1)
    c: Coincident(g1,g2)
    c: Vertical(g0)
    c: Vertical(g2)
    c: DistanceX(g0,g6) = 20.5
    c: DistanceY(g1,g-1) = 6
    c: Symmetric(g1,g0,g-2)
    c: Coincident(g4,g6)
    c: Coincident(g4,g3)
    c: Coincident(g5,g4)
    c: Coincident(g5,g0)
    c: DistanceY(g-1,g0) = 9.5
    c: Distance(g6,g3) = 30
    c: DistanceY(g-1,g6) = 11
    c: Angle(g3,g5) = 0.349066
    c: Coincident(g2,g4)
    c: Coincident(g3,g2)
    c: Angle(g3,g-1) = 0.296706
FEATURE [PartDesign::SubShapeBinder] Binder
  BindCopyOnChange = 0
  BindMode = 0
  ClaimChildren = false
  Context = -> Part001 [Body.Binder.]
  Fuse = false
  MakeFace = true
  OffsetFill = false
  OffsetIntersection = false
  OffsetJoinType = 0
  OffsetOpenResult = false
  PartialLoad = false
  Placement = pos=(14,-11,-3.25) rot=(0,0,1;2.87979rad)
  Refine = true
  Relative = true
  Support = -> [Sketch006]
  _Version = 2
FEATURE [PartDesign::SubShapeBinder] Binder001
  BindCopyOnChange = 0
  BindMode = 0
  ClaimChildren = false
  Context = -> Part001 [Body.Binder001.]
  Fuse = false
  MakeFace = true
  OffsetFill = false
  OffsetIntersection = false
  OffsetJoinType = 0
  OffsetOpenResult = false
  PartialLoad = false
  Placement = pos=(48,-22,-3.25) rot=(0,0,1;0.349066rad)
  Refine = true
  Relative = true
  Support = -> [Sketch006]
  _Version = 2
FEATURE [Sketcher::SketchObject] Sketch007  label="KW12ScrewholeBase"
  ArcFitTolerance = 1e-06
  AttachmentSupport = -> [XY_Plane003]
  FullyConstrained = true
  MakeInternals = false
  MapMode = 5
  sketch-geometry (2):
    g0: Circle CenterX=-4.75 CenterY=2.9 CenterZ=0 NormalX=0 NormalY=0 NormalZ=1 AngleXU=0 Radius=1
    g1: Circle CenterX=4.75 CenterY=2.9 CenterZ=0 NormalX=0 NormalY=0 NormalZ=1 AngleXU=0 Radius=1
  constraints (5):
    c: Symmetric(g1,g0,g-2)
    c: DistanceY(g-1,g1) = 2.9
    c: DistanceX(g0,g1) = 9.5
    c: Equal(g1,g0)
    c: Diameter(g1) = 2
FEATURE [PartDesign::SubShapeBinder] Binder002  label="TriggerSwitchScrewHolderBinder"
  BindCopyOnChange = 0
  BindMode = 0
  ClaimChildren = false
  Context = -> Part001 [Body.Binder002.]
  Fuse = false
  MakeFace = true
  OffsetFill = false
  OffsetIntersection = false
  OffsetJoinType = 0
  OffsetOpenResult = false
  PartialLoad = false
  Placement = pos=(14,-11,0) rot=(0,0,1;2.87979rad)
  Refine = true
  Relative = true
  Support = -> [Sketch007]
  _Version = 2
FEATURE [PartDesign::SubShapeBinder] Binder003
  BindCopyOnChange = 0
  BindMode = 0
  ClaimChildren = false
  Context = -> Part001 [Body.Binder003.]
  Fuse = false
  MakeFace = true
  OffsetFill = false
  OffsetIntersection = false
  OffsetJoinType = 0
  OffsetOpenResult = false
  PartialLoad = false
  Placement = pos=(48,-22,0) rot=(0,0,1;0.349066rad)
  Refine = true
  Relative = true
  Support = -> [Sketch007]
  _Version = 2
FEATURE [Sketcher::SketchObject] Sketch008
  ArcFitTolerance = 1e-06
  AttachmentOffset = pos=(0,0,6.25) rot=(0,0,1;0rad)
  AttachmentSupport = -> [XY_Plane003]
  FullyConstrained = true
  MakeInternals = false
  MapMode = 5
  Placement = pos=(0,0,6.25) rot=(0,0,1;0rad)
  sketch-geometry (8):
    g0: LineSegment StartX=20 StartY=-19 StartZ=0 EndX=19.4824 EndY=-20.9319 EndZ=0
    g1: LineSegment StartX=19.4824 StartY=-20.9319 StartZ=0 EndX=40.7327 EndY=-26.6259 EndZ=0
    g2: LineSegment StartX=40.7327 StartY=-26.6259 StartZ=0 EndX=41.2504 EndY=-24.694 EndZ=0
    g3: LineSegment StartX=41.2504 StartY=-24.694 StartZ=0 EndX=20 EndY=-19 EndZ=0
    g4: LineSegment StartX=50 StartY=-10.5 StartZ=0 EndX=50 EndY=-14.5 EndZ=0
    g5: LineSegment StartX=50 StartY=-14.5 StartZ=0 EndX=75 EndY=-14.5 EndZ=0
    g6: LineSegment StartX=75 StartY=-14.5 StartZ=0 EndX=75 EndY=-10.5 EndZ=0
    g7: LineSegment StartX=75 StartY=-10.5 StartZ=0 EndX=50 EndY=-10.5 EndZ=0
  constraints (24):
    c: Coincident(g0,g1)
    c: Coincident(g1,g2)
    c: Coincident(g2,g3)
    c: Coincident(g3,g0)
    c: Parallel(g0,g2)
    c: Parallel(g1,g3)
    c: Distance(g0,g0) = 2
    c: Perpendicular(g0,g1)
    c: Angle(g3,g-1) = 0.261799
    c: DistanceX(g-1,g0) = 20
    c: DistanceY(g0,g-1) = 19
    c: Distance(g1,g1) = 22
    c: Coincident(g4,g5)
    c: Coincident(g5,g6)
    c: Coincident(g6,g7)
    c: Coincident(g7,g4)
    c: Vertical(g4)
    c: Vertical(g6)
    c: Horizontal(g5)
    c: Horizontal(g7)
    c: DistanceX(g-1,g6) = 75
    c: DistanceX(g7,g7) = 25
    c: DistanceY(g6,g-1) = 10.5
    c: DistanceY(g4,g4) = 4
FEATURE [Sketcher::SketchObject] Sketch009
  ArcFitTolerance = 1e-06
  AttachmentOffset = pos=(0,0,-4) rot=(0,0,1;0rad)
  AttachmentSupport = -> [XY_Plane003]
  FullyConstrained = true
  MakeInternals = false
  MapMode = 5
  Placement = pos=(0,0,-4) rot=(0,0,1;0rad)
  sketch-geometry (3):
    g0: Circle [constr] CenterX=35 CenterY=-6 CenterZ=0 NormalX=0 NormalY=0 NormalZ=1 AngleXU=0 Radius=5
    g1: ArcOfCircle CenterX=35 CenterY=-6 CenterZ=0 NormalX=0 NormalY=0 NormalZ=1 AngleXU=0 Radius=5 StartAngle=2.2143 EndAngle=7.21048
    g2: LineSegment StartX=32 StartY=-2 StartZ=0 EndX=38 EndY=-2 EndZ=0
  constraints (9):
    c: Diameter(g0) = 10
    c: DistanceY(g0,g-1) = 6
    c: DistanceX(g-1,g0) = 35
    c: Coincident(g1,g0)
    c: PointOnObject(g1,g0)
    c: Coincident(g2,g1)
    c: Coincident(g2,g1)
    c: DistanceY(g1,g-1) = 2
    c: Horizontal(g2)
FEATURE [PartDesign::Pad] Pad002  label="LoadingLeverBush"
  BaseFeature = -> Pocket003
  Direction = (0,0,1)
  Length = 10
  Length2 = 10
  Profile = -> Sketch009
  ReferenceAxis = -> Sketch009 [N_Axis]
  Refine = true
  Reversed = true
  Suppressed = false
  Type = 2
FEATURE [Sketcher::SketchObject] Sketch010
  ArcFitTolerance = 1e-06
  AttachmentSupport = -> [XY_Plane003]
  FullyConstrained = true
  MakeInternals = false
  MapMode = 5
  sketch-geometry (1):
    g0: Circle CenterX=35 CenterY=-6 CenterZ=0 NormalX=0 NormalY=0 NormalZ=1 AngleXU=0 Radius=1.25
  constraints (3):
    c: Diameter(g0) = 2.5
    c: DistanceX(g-1,g0) = 35
    c: DistanceY(g0,g-1) = 6
FEATURE [PartDesign::Pocket] Pocket009  label="LoadingLeverBoltHole"
  BaseFeature = -> Pad002
  Direction = (0,0,-1)
  Length = 5
  Length2 = 5
  Midplane = true
  Profile = -> Sketch010
  ReferenceAxis = -> Sketch010 [N_Axis]
  Refine = true
  Suppressed = false
  Type = 1
FEATURE [PartDesign::Pocket] Pocket004  label="TriggerSwitchcutout"
  BaseFeature = -> Pocket009
  Direction = (0,0,-1)
  Length = 5
  Length2 = 5
  Profile = -> Binder
  Refine = true
  Reversed = true
  Suppressed = false
  Type = 1
FEATURE [PartDesign::Pocket] Pocket005  label="LoadingSwitchCutout"
  BaseFeature = -> Pocket004
  Direction = (0,0,-1)
  Length = 5
  Length2 = 5
  Profile = -> Binder001
  Refine = true
  Reversed = true
  Suppressed = false
  Type = 1
FEATURE [PartDesign::Pocket] Pocket006  label="TriggerSwitchScrewHoles"
  BaseFeature = -> Pocket005
  Direction = (0,0,-1)
  Length = 5
  Length2 = 5
  Midplane = true
  Profile = -> Binder002
  Refine = true
  Suppressed = false
  Type = 1
FEATURE [PartDesign::Pocket] Pocket007  label="LoadingSwitchScrewHoles"
  BaseFeature = -> Pocket006
  Direction = (0,0,-1)
  Length = 5
  Length2 = 5
  Midplane = true
  Profile = -> Binder003
  Refine = true
  Suppressed = false
  Type = 1
FEATURE [PartDesign::Pocket] Pocket008  label="WireRun"
  BaseFeature = -> Pocket007
  Direction = (0,0,-1)
  Length = 3
  Length2 = 5
  Profile = -> Sketch008
  ReferenceAxis = -> Sketch008 [N_Axis]
  Refine = true
  Suppressed = false
  TaperAngle = -10
  Type = 0
FEATURE [PartDesign::Body] Body
  AllowCompound = false
  Group = -> [Sketch,Pad,Sketch001,Pocket,Sketch002,Pad001,Sketch003,Pocket001,Sketch004,Pocket002,Sketch005,Pocket003,Sketch006,Binder,Sketch009,Pad002,Sketch010,Pocket009,Pocket004,Binder001,Pocket005,Sketch007,Binder002,Pocket006,Binder003,Pocket007,Sketch008,Pocket008]
  Origin = -> Origin003
  Tip = -> Pocket008
FEATURE [App::Part] Part001  label="TriggerPlate.stl"
  Group = -> [Body]
  Origin = -> Origin004
